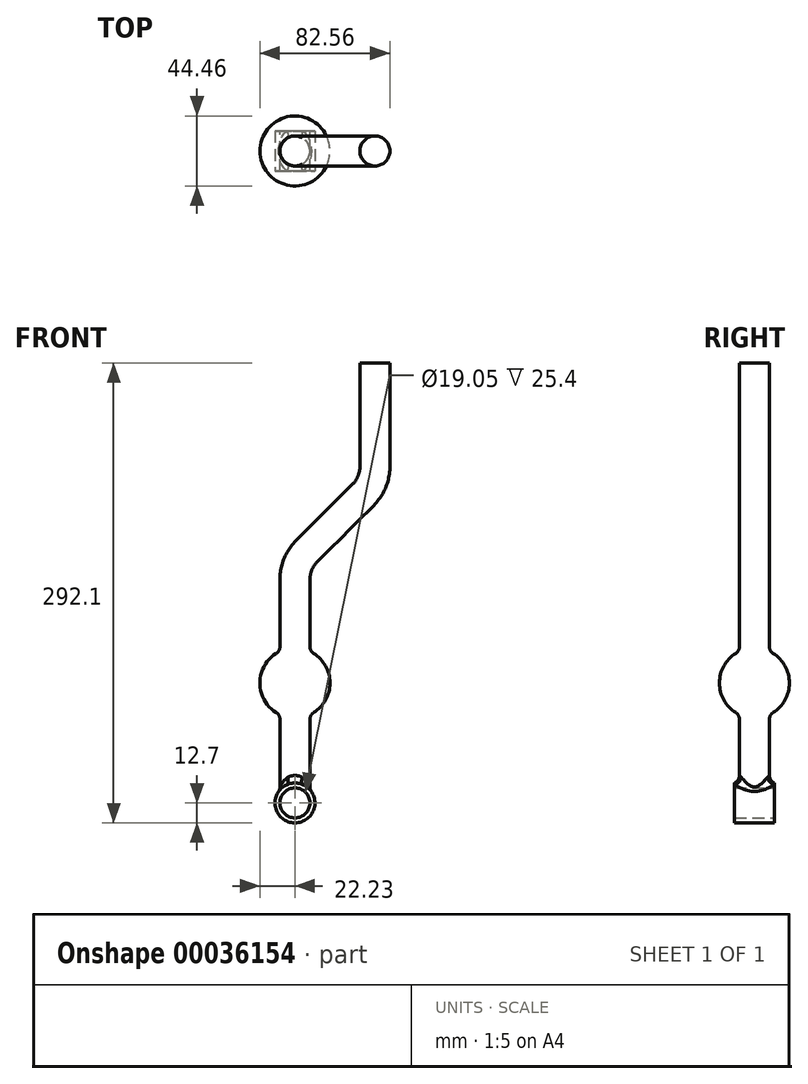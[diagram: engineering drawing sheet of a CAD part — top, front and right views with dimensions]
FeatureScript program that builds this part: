
annotation { "Feature Type Name" : "Feature", "Feature Type Description" : "" }
export const myFeature = defineFeature(function(context is Context, id is Id, definition is map)
    precondition{}
    {
        {
            var Q0;
            Q0=qCreatedBy(makeId("Front.planeOp"),FACE);
            var sketch = newSketch(context, id + "F0", { "sketchPlane" : qUnion([Q0])});
            skLineSegment(sketch, "E0", {"start": v(7.44, 83.64) * mm, "end": v(43.36, 119.56) * mm});
            skLineSegment(sketch, "E1", {"start": v(50.8, 137.52) * mm, "end": v(50.8, 203.2) * mm});
            skPoint(sketch, "E2.center.orphan", {"position": v(0, 0) * mm});
            skLineSegment(sketch, "E3.trimOffspring", {"start": v(0, 0) * mm, "end": v(0, 65.68) * mm});
            skPoint(sketch, "E4.visualSharp", {"position": v(0, 76.2) * mm});
            skArc(sketch, "E4.filletArc", {"start": v(7.44, 83.64) * mm, "mid": v(1.93, 75.4) * mm, "end": v(0, 65.68) * mm});
            skPoint(sketch, "E5.visualSharp", {"position": v(50.8, 127) * mm});
            skArc(sketch, "E5.filletArc", {"start": v(43.36, 119.56) * mm, "mid": v(48.87, 127.8) * mm, "end": v(50.8, 137.52) * mm});
            skSolve(sketch);
        }
        {
            var Q0;
            Q0=qCreatedBy(makeId("Top.planeOp"),FACE);
            var sketch = newSketch(context, id + "F1", { "sketchPlane" : qUnion([Q0])});
            skCircle(sketch, "E6", {"center": v(0, 0) * mm, "radius": 9.52 * mm});
            skSolve(sketch);
        }
        {
            var Q0;
            Q0=makeQuery(id+"F1.imprint","IMPRINT",FACE,{"disambiguationData":[TD([[makeQuery(id+"F1.imprint","IMPRINT",EDGE,{"derivedFrom":sQuery(id+"F1.wireOp",EDGE,"E6")}),1.0]])]});
            var Q1;
            Q1=sQuery(id+"F0.wireOp",EDGE,"E3.trimOffspring");
            var Q2;
            Q2=sQuery(id+"F0.wireOp",EDGE,"E4.filletArc");
            var Q3;
            Q3=sQuery(id+"F0.wireOp",EDGE,"E0");
            var Q4;
            Q4=sQuery(id+"F0.wireOp",EDGE,"E5.filletArc");
            var Q5;
            Q5=sQuery(id+"F0.wireOp",EDGE,"E1");
            sweep(context, id + "F2", {"profiles" : qUnion([Q0]), "path" : qUnion([Q1, Q2, Q3, Q4, Q5])});
        }
        {
            var Q0;
            Q0=qCreatedBy(makeId("Front.planeOp"),FACE);
            var sketch = newSketch(context, id + "F3", { "sketchPlane" : qUnion([Q0])});
            skArc(sketch, "E7", {"start": v(0, -22.23) * mm, "mid": v(22.23, 0) * mm, "end": v(0, 22.23) * mm});
            skLineSegment(sketch, "E8", {"start": v(0, 22.23) * mm, "end": v(0, -22.23) * mm});
            skSolve(sketch);
        }
        {
            var Q0;
            Q0=qCreatedBy(makeId("Front.planeOp"),FACE);
            var sketch = newSketch(context, id + "F4", { "sketchPlane" : qUnion([Q0])});
            skLineSegment(sketch, "E9", {"start": v(0, 0) * mm, "end": v(0, -76.2) * mm});
            skSolve(sketch);
        }
        {
            var Q0;
            Q0=makeQuery(id+"F2.opSweep","CAP_FACE",FACE,{"disambiguationData":[OSD([sQuery(id+"F0.wireOp",VERTEX,"E3.trimOffspring.start"),sQuery(id+"F1.wireOp",EDGE,"E6")])],"isStart":true});
            var Q1;
            Q1=sQuery(id+"F4.wireOp",EDGE,"E9");
            sweep(context, id + "F5", {"operationType" : NewBodyOperationType.ADD, "profiles" : qUnion([Q0]), "path" : qUnion([Q1])});
        }
        {
            var Q0;
            Q0=makeQuery(id+"F3.imprint","IMPRINT",FACE,{"disambiguationData":[TD([[makeQuery(id+"F3.imprint","IMPRINT",EDGE,{"derivedFrom":sQuery(id+"F3.wireOp",EDGE,"E7")}),1.0]])]});
            var Q1;
            Q1=sQuery(id+"F3.wireOp",EDGE,"E8");
            revolve(context, id + "F7", {"operationType" : NewBodyOperationType.ADD, "entities" : qUnion([Q0]), "axis" : qUnion([Q1]), "revolveType" : RevolveType.FULL});
        }
        {
            var Q0;
            Q0=qCreatedBy(makeId("Front.planeOp"),FACE);
            var sketch = newSketch(context, id + "F8", { "sketchPlane" : qUnion([Q0])});
            skLineSegment(sketch, "E10.0", {"start": v(9.52, -76.2) * mm, "end": v(-9.52, -76.2) * mm});
            skCircle(sketch, "E11", {"center": v(0, -76.2) * mm, "radius": 12.7 * mm});
            skSolve(sketch);
        }
        {
            var Q0;
            Q0=makeQuery(id+"F8.imprint","IMPRINT",FACE,{"disambiguationData":[TD([[makeQuery(id+"F8.imprint","IMPRINT",EDGE,{"derivedFrom":sQuery(id+"F8.wireOp",EDGE,"E11")}),1.0]])]});
            extrude(context, id + "F9", {"entities" : qUnion([Q0]), "operationType" : NewBodyOperationType.ADD, "endBound" : BoundingType.SYMMETRIC, "oppositeDirection" : true, "depth" : 25.4 * mm});
        }
        {
            var Q0;
            Q0=makeQuery(id+"F9.opExtrude","CAP_FACE",FACE,{"disambiguationData":[OSD([sQuery(id+"F8.wireOp",EDGE,"E11")])],"isStart":false});
            var sketch = newSketch(context, id + "F6", { "sketchPlane" : qUnion([Q0])});
            skCircle(sketch, "E12", {"center": v(0, -76.2) * mm, "radius": 9.53 * mm});
            skSolve(sketch);
        }
        {
            var Q0;
            Q0=makeQuery(id+"F6.imprint","IMPRINT",FACE,{"disambiguationData":[TD([[makeQuery(id+"F6.imprint","IMPRINT",EDGE,{"derivedFrom":sQuery(id+"F6.wireOp",EDGE,"E12")}),1.0]])]});
            extrude(context, id + "F10", {"entities" : qUnion([Q0]), "operationType" : NewBodyOperationType.REMOVE, "oppositeDirection" : true, "depth" : 25.4 * mm});
        }
        {
            var Q0;
            {var subQ0=sQuery(id+"F1.wireOp",EDGE,"E6");var subQ1=sQuery(id+"F0.wireOp",VERTEX,"E3.trimOffspring.start");Q0=makeQuery(id+"F7.boolean.opBoolean","SPLIT",FACE,{"disambiguationData":[TD([makeQuery(id+"F5.opSweep","CAP_FACE",FACE,{"disambiguationData":[OSD([subQ1,subQ0,sQuery(id+"F4.wireOp",VERTEX,"E9.end")])],"isStart":false})])],"derivedFrom":makeQuery(id+"F5.boolean.opBoolean","MERGE",FACE,{"derivedFrom":[makeQuery(id+"F2.opSweep","SWEPT_FACE",FACE,{"disambiguationData":[OSD([sQuery(id+"F0.wireOp",EDGE,"E3.trimOffspring"),subQ0])]}),makeQuery(id+"F5.opSweep","SWEPT_FACE",FACE,{"disambiguationData":[OSD([subQ1,subQ0,sQuery(id+"F4.wireOp",EDGE,"E9")])]})]})});}
            var Q1;
            Q1=makeQuery(id+"F7.opRevolve","SWEPT_FACE",FACE,{"disambiguationData":[OSD([sQuery(id+"F3.wireOp",EDGE,"E7")])]});
            fillet(context, id + "F11", {"entities" : qUnion([Q0, Q1]), "radius" : 5.08 * mm, "tangentPropagation" : true, "allowEdgeOverflow" : false});
        }
    });
